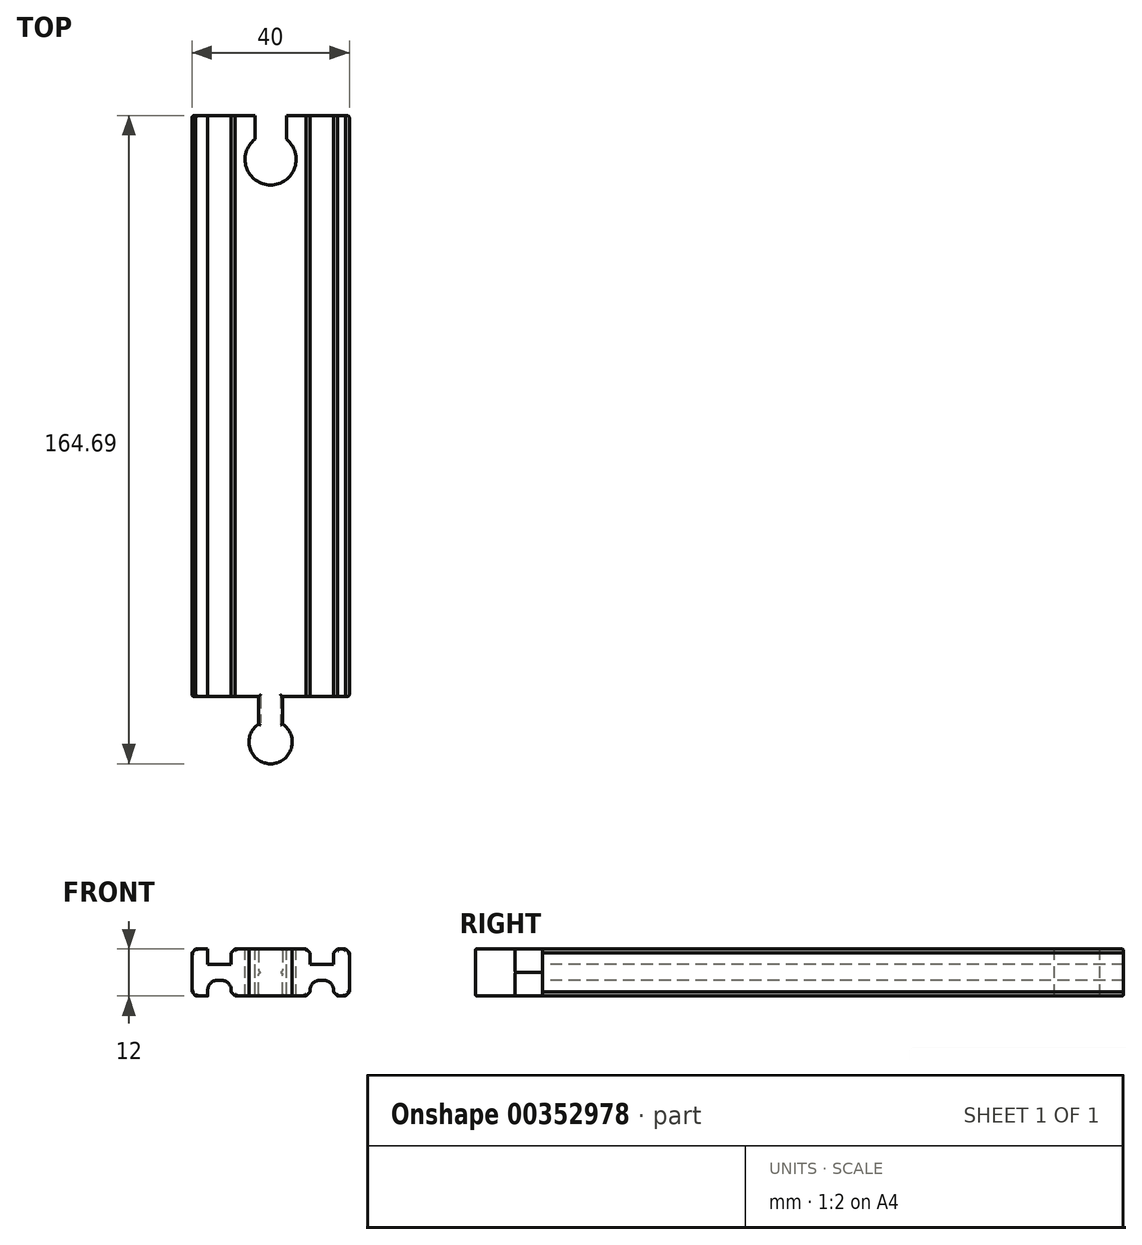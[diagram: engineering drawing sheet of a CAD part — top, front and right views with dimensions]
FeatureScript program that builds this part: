
annotation { "Feature Type Name" : "Feature", "Feature Type Description" : "" }
export const myFeature = defineFeature(function(context is Context, id is Id, definition is map)
    precondition{}
    {
        {
            var Q0;
            Q0=qCreatedBy(makeId("Top.planeOp"),FACE);
            var sketch = newSketch(context, id + "F0", { "sketchPlane" : qUnion([Q0])});
            skLineSegment(sketch, "E0.bottom", {"start": v(20, 73.79) * mm, "end": v(-20, 73.79) * mm});
            skLineSegment(sketch, "E0.top", {"start": v(20, -73.79) * mm, "end": v(-20, -73.79) * mm});
            skLineSegment(sketch, "E0.left", {"start": v(20, 73.79) * mm, "end": v(20, -73.79) * mm});
            skLineSegment(sketch, "E0.right", {"start": v(-20, 73.79) * mm, "end": v(-20, -73.79) * mm});
            skPoint(sketch, "E0.middle", {"position": v(0, 0) * mm});
            skLineSegment(sketch, "E1", {"start": v(-3, -73.79) * mm, "end": v(-3, -80.79) * mm});
            skLineSegment(sketch, "E2", {"start": v(3, -73.79) * mm, "end": v(3, -80.79) * mm});
            skCircle(sketch, "E3", {"center": v(0, -85.4) * mm, "radius": 5.5 * mm});
            skPoint(sketch, "E3.centerSnap0", {"position": v(0, -73.79) * mm});
            skSolve(sketch);
        }
        {
            var Q0;
            Q0=makeQuery(id+"F0.imprint","IMPRINT",FACE,{"disambiguationData":[TD([[makeQuery(id+"F0.imprint","IMPRINT",EDGE,{"derivedFrom":sQuery(id+"F0.wireOp",EDGE,"E0.bottom")}),1.0]])]});
            var Q1;
            {var subQ0=sQuery(id+"F0.wireOp",EDGE,"E1");Q1=makeQuery(id+"F0.imprint","IMPRINT",FACE,{"disambiguationData":[TD([[makeQuery(id+"F0.imprint","IMPRINT",EDGE,{"derivedFrom":subQ0}),1.0]])]});}
            var Q2;
            {var subQ0=sQuery(id+"F0.wireOp",EDGE,"E3");var subQ1=makeQuery(id+"F0.imprint","INTERSECT",VERTEX,{"derivedFrom":[sQuery(id+"F0.wireOp",EDGE,"E1"),subQ0]});Q2=makeQuery(id+"F0.imprint","IMPRINT",FACE,{"disambiguationData":[TD([[makeQuery(id+"F0.imprint","IMPRINT",EDGE,{"disambiguationData":[TD([[subQ1,1.0]])],"derivedFrom":subQ0}),1.0]])]});}
            extrude(context, id + "F1", {"entities" : qUnion([Q0, Q1, Q2]), "offsetDistance" : 25 * mm, "depth" : 6 * mm});
        }
        {
            var Q0;
            Q0=makeQuery(id+"F1.opExtrude","CAP_FACE",FACE,{"disambiguationData":[OSD([sQuery(id+"F0.wireOp",EDGE,"E0.bottom"),sQuery(id+"F0.wireOp",EDGE,"E0.top"),sQuery(id+"F0.wireOp",EDGE,"E0.left"),sQuery(id+"F0.wireOp",EDGE,"E0.right"),sQuery(id+"F0.wireOp",EDGE,"E1"),sQuery(id+"F0.wireOp",EDGE,"E2"),sQuery(id+"F0.wireOp",EDGE,"E3")])],"isStart":false});
            var sketch = newSketch(context, id + "F2", { "sketchPlane" : qUnion([Q0])});
            skLineSegment(sketch, "E4", {"start": v(-4, 73.79) * mm, "end": v(-4, 67.79) * mm});
            skLineSegment(sketch, "E5", {"start": v(4, 73.79) * mm, "end": v(4, 67.79) * mm});
            skCircle(sketch, "E6", {"center": v(0, 62.66) * mm, "radius": 6.5 * mm});
            skSolve(sketch);
        }
        {
            var Q0;
            {var subQ0=sQuery(id+"F2.wireOp",EDGE,"E6");var subQ1=makeQuery(id+"F2.imprint","INTERSECT",VERTEX,{"derivedFrom":[sQuery(id+"F2.wireOp",EDGE,"E4"),subQ0]});Q0=makeQuery(id+"F2.imprint","IMPRINT",FACE,{"disambiguationData":[TD([[makeQuery(id+"F2.imprint","IMPRINT",EDGE,{"disambiguationData":[TD([[subQ1,1.0]])],"derivedFrom":subQ0}),1.0]])]});}
            var Q1;
            {var subQ0=sQuery(id+"F2.wireOp",EDGE,"E4");Q1=makeQuery(id+"F2.imprint","IMPRINT",FACE,{"disambiguationData":[TD([[makeQuery(id+"F2.imprint","IMPRINT",EDGE,{"derivedFrom":subQ0}),1.0]])]});}
            extrude(context, id + "F3", {"entities" : qUnion([Q0, Q1]), "operationType" : NewBodyOperationType.REMOVE, "oppositeDirection" : true, "depth" : 12 * mm});
        }
        {
            var Q0;
            Q0=makeQuery(id+"F1.opExtrude","CAP_FACE",FACE,{"disambiguationData":[OSD([sQuery(id+"F0.wireOp",EDGE,"E0.bottom"),sQuery(id+"F0.wireOp",EDGE,"E0.top"),sQuery(id+"F0.wireOp",EDGE,"E0.left"),sQuery(id+"F0.wireOp",EDGE,"E0.right"),sQuery(id+"F0.wireOp",EDGE,"E1"),sQuery(id+"F0.wireOp",EDGE,"E2"),sQuery(id+"F0.wireOp",EDGE,"E3")])],"isStart":false});
            var sketch = newSketch(context, id + "F4", { "sketchPlane" : qUnion([Q0])});
            skLineSegment(sketch, "E7.bottom", {"start": v(-16, 73.79) * mm, "end": v(-10, 73.79) * mm});
            skLineSegment(sketch, "E7.top", {"start": v(-16, -73.79) * mm, "end": v(-10, -73.79) * mm});
            skLineSegment(sketch, "E7.left", {"start": v(-16, 73.79) * mm, "end": v(-16, -73.79) * mm});
            skLineSegment(sketch, "E7.right", {"start": v(-10, 73.79) * mm, "end": v(-10, -73.79) * mm});
            skLineSegment(sketch, "E8.bottom", {"start": v(10, 73.79) * mm, "end": v(16, 73.79) * mm});
            skLineSegment(sketch, "E8.top", {"start": v(10, -73.79) * mm, "end": v(16, -73.79) * mm});
            skLineSegment(sketch, "E8.left", {"start": v(10, 73.79) * mm, "end": v(10, -73.79) * mm});
            skLineSegment(sketch, "E8.right", {"start": v(16, 73.79) * mm, "end": v(16, -73.79) * mm});
            skSolve(sketch);
        }
        {
            var Q0;
            Q0 = qSketchRegion(id + "F4", true);
            extrude(context, id + "F5", {"entities" : qUnion([Q0]), "operationType" : NewBodyOperationType.REMOVE, "oppositeDirection" : true, "depth" : 4 * mm});
        }
        {
            var Q0;
            Q0=makeQuery(id+"F1.opExtrude","CAP_EDGE",EDGE,{"disambiguationData":[OSD([sQuery(id+"F0.wireOp",EDGE,"E0.right")])],"isStart":false});
            var Q1;
            Q1=makeQuery(id+"F5.boolean.opBoolean","COPY",EDGE,{"derivedFrom":makeQuery(id+"F5.opExtrude","CAP_EDGE",EDGE,{"disambiguationData":[OSD([sQuery(id+"F4.wireOp",EDGE,"E7.left")])],"isStart":true})});
            var Q2;
            Q2=makeQuery(id+"F5.boolean.opBoolean","COPY",EDGE,{"derivedFrom":makeQuery(id+"F5.opExtrude","CAP_EDGE",EDGE,{"disambiguationData":[OSD([sQuery(id+"F4.wireOp",EDGE,"E7.right")])],"isStart":true})});
            var Q3;
            Q3=makeQuery(id+"F5.boolean.opBoolean","COPY",EDGE,{"derivedFrom":makeQuery(id+"F5.opExtrude","CAP_EDGE",EDGE,{"disambiguationData":[OSD([sQuery(id+"F4.wireOp",EDGE,"E8.right")])],"isStart":true})});
            var Q4;
            Q4=makeQuery(id+"F1.opExtrude","CAP_EDGE",EDGE,{"disambiguationData":[OSD([sQuery(id+"F0.wireOp",EDGE,"E0.left")])],"isStart":false});
            var Q5;
            Q5=makeQuery(id+"F5.boolean.opBoolean","COPY",EDGE,{"derivedFrom":makeQuery(id+"F5.opExtrude","CAP_EDGE",EDGE,{"disambiguationData":[OSD([sQuery(id+"F4.wireOp",EDGE,"E8.left")])],"isStart":true})});
            chamfer(context, id + "F6", {"entities" : qUnion([Q0, Q1, Q2, Q3, Q4, Q5]), "width" : 1 * mm, "tangentPropagation" : true});
        }
        {
            var Q0;
            Q0=makeQuery(id+"F1.opExtrude","CAP_EDGE",EDGE,{"disambiguationData":[OSD([sQuery(id+"F0.wireOp",EDGE,"E3")])],"isStart":false});
            var Q1;
            Q1=makeQuery(id+"F1.opExtrude","CAP_EDGE",EDGE,{"disambiguationData":[OSD([sQuery(id+"F0.wireOp",EDGE,"E1")])],"isStart":true});
            var Q2;
            Q2=makeQuery(id+"F1.opExtrude","CAP_EDGE",EDGE,{"disambiguationData":[OSD([sQuery(id+"F0.wireOp",EDGE,"E2")])],"isStart":true});
            var Q3;
            Q3=makeQuery(id+"F1.opExtrude","CAP_EDGE",EDGE,{"disambiguationData":[OSD([sQuery(id+"F0.wireOp",EDGE,"E1")])],"isStart":false});
            var Q4;
            Q4=makeQuery(id+"F1.opExtrude","CAP_EDGE",EDGE,{"disambiguationData":[OSD([sQuery(id+"F0.wireOp",EDGE,"E2")])],"isStart":false});
            var Q5;
            Q5=makeQuery(id+"F3.boolean.opBoolean","COPY",EDGE,{"derivedFrom":makeQuery(id+"F3.opExtrude","CAP_EDGE",EDGE,{"disambiguationData":[OSD([sQuery(id+"F2.wireOp",EDGE,"E6")])],"isStart":true})});
            var Q6;
            Q6=makeQuery(id+"F3.boolean.opBoolean","COPY",EDGE,{"derivedFrom":makeQuery(id+"F3.opExtrude","CAP_EDGE",EDGE,{"disambiguationData":[OSD([sQuery(id+"F2.wireOp",EDGE,"E4")])],"isStart":true})});
            var Q7;
            Q7=makeQuery(id+"F3.boolean.opBoolean","COPY",EDGE,{"derivedFrom":makeQuery(id+"F3.opExtrude","CAP_EDGE",EDGE,{"disambiguationData":[OSD([sQuery(id+"F2.wireOp",EDGE,"E5")])],"isStart":true})});
            var Q8;
            Q8=makeQuery(id+"F3.boolean.opBoolean","COPY",EDGE,{"derivedFrom":makeQuery(id+"F3.opExtrude","CAP_EDGE",EDGE,{"disambiguationData":[OSD([sQuery(id+"F2.wireOp",EDGE,"E4")])],"isStart":false})});
            var Q9;
            Q9=makeQuery(id+"F3.boolean.opBoolean","COPY",EDGE,{"derivedFrom":makeQuery(id+"F3.opExtrude","CAP_EDGE",EDGE,{"disambiguationData":[OSD([sQuery(id+"F2.wireOp",EDGE,"E5")])],"isStart":false})});
            var Q10;
            Q10=makeQuery(id+"F3.boolean.opBoolean","COPY",EDGE,{"derivedFrom":makeQuery(id+"F3.opExtrude","CAP_EDGE",EDGE,{"disambiguationData":[OSD([sQuery(id+"F2.wireOp",EDGE,"E6")])],"isStart":false})});
            var Q11;
            Q11=makeQuery(id+"F1.opExtrude","SWEPT_EDGE",EDGE,{"disambiguationData":[OSD([sQuery(id+"F0.wireOp",EDGE,"E0.top"),sQuery(id+"F0.wireOp",EDGE,"E0.right")])]});
            var Q12;
            {var subQ0=sQuery(id+"F0.wireOp",EDGE,"E0.right");var subQ1=sQuery(id+"F0.wireOp",EDGE,"E0.top");Q12=makeQuery(id+"F6.opChamfer","BLEND_EDGE",EDGE,{"blendedFrom":[makeQuery(id+"F1.opExtrude","CAP_EDGE",EDGE,{"disambiguationData":[OSD([subQ0])],"isStart":false}),makeQuery(id+"F1.opExtrude","SWEPT_FACE",FACE,{"disambiguationData":[OSD([subQ1]),TDD([makeQuery(id+"F0.imprint","IMPRINT",EDGE,{"disambiguationData":[TD([[makeQuery(id+"F0.imprint","INTERSECT",VERTEX,{"derivedFrom":[subQ1,subQ0]}),1.0]])],"derivedFrom":subQ1})])]})],"blendedInto":[makeQuery(id+"F1.opExtrude","SWEPT_FACE",FACE,{"disambiguationData":[OSD([subQ1]),TDD([makeQuery(id+"F0.imprint","IMPRINT",EDGE,{"disambiguationData":[TD([[makeQuery(id+"F0.imprint","INTERSECT",VERTEX,{"derivedFrom":[subQ1,subQ0]}),1.0]])],"derivedFrom":subQ1})])]})]});}
            var Q13;
            Q13=makeQuery(id+"F5.boolean.opBoolean","COPY",EDGE,{"derivedFrom":makeQuery(id+"F5.opExtrude","CAP_EDGE",EDGE,{"disambiguationData":[OSD([sQuery(id+"F4.wireOp",EDGE,"E7.top")])],"isStart":false})});
            var Q14;
            Q14=makeQuery(id+"F5.boolean.opBoolean","COPY",EDGE,{"derivedFrom":makeQuery(id+"F5.opExtrude","SWEPT_EDGE",EDGE,{"disambiguationData":[OSD([sQuery(id+"F0.wireOp",EDGE,"E0.top"),sQuery(id+"F4.wireOp",EDGE,"E7.top"),sQuery(id+"F4.wireOp",EDGE,"E7.left")])]})});
            var Q15;
            {var subQ0=sQuery(id+"F0.wireOp",EDGE,"E0.top");Q15=makeQuery(id+"F6.opChamfer","BLEND_EDGE",EDGE,{"blendedFrom":[makeQuery(id+"F5.boolean.opBoolean","COPY",EDGE,{"derivedFrom":makeQuery(id+"F5.opExtrude","CAP_EDGE",EDGE,{"disambiguationData":[OSD([sQuery(id+"F4.wireOp",EDGE,"E7.left")])],"isStart":true})}),makeQuery(id+"F1.opExtrude","SWEPT_FACE",FACE,{"disambiguationData":[OSD([subQ0]),TDD([makeQuery(id+"F0.imprint","IMPRINT",EDGE,{"disambiguationData":[TD([[makeQuery(id+"F0.imprint","INTERSECT",VERTEX,{"derivedFrom":[subQ0,sQuery(id+"F0.wireOp",EDGE,"E0.right")]}),1.0]])],"derivedFrom":subQ0})])]})],"blendedInto":[makeQuery(id+"F1.opExtrude","SWEPT_FACE",FACE,{"disambiguationData":[OSD([subQ0]),TDD([makeQuery(id+"F0.imprint","IMPRINT",EDGE,{"disambiguationData":[TD([[makeQuery(id+"F0.imprint","INTERSECT",VERTEX,{"derivedFrom":[subQ0,sQuery(id+"F0.wireOp",EDGE,"E0.right")]}),1.0]])],"derivedFrom":subQ0})])]})]});}
            var Q16;
            {var subQ1=sQuery(id+"F0.wireOp",EDGE,"E0.right");var subQ2=sQuery(id+"F0.wireOp",EDGE,"E0.top");var subQ3=makeQuery(id+"F0.imprint","IMPRINT",EDGE,{"disambiguationData":[TD([[makeQuery(id+"F0.imprint","INTERSECT",VERTEX,{"derivedFrom":[subQ2,subQ1]}),1.0]])],"derivedFrom":subQ2});Q16=makeQuery(id+"F5.boolean.opBoolean","SPLIT",EDGE,{"disambiguationData":[TD([makeQuery(id+"F1.opExtrude","SWEPT_FACE",FACE,{"disambiguationData":[OSD([subQ1])]})])],"derivedFrom":makeQuery(id+"F1.opExtrude","CAP_EDGE",EDGE,{"disambiguationData":[OSD([subQ2]),TDD([subQ3])],"isStart":false})});}
            var Q17;
            Q17=makeQuery(id+"F5.boolean.opBoolean","COPY",EDGE,{"derivedFrom":makeQuery(id+"F5.opExtrude","SWEPT_EDGE",EDGE,{"disambiguationData":[OSD([sQuery(id+"F0.wireOp",EDGE,"E0.top"),sQuery(id+"F4.wireOp",EDGE,"E7.top"),sQuery(id+"F4.wireOp",EDGE,"E7.right")])]})});
            var Q18;
            {var subQ0=sQuery(id+"F0.wireOp",EDGE,"E0.top");Q18=makeQuery(id+"F6.opChamfer","BLEND_EDGE",EDGE,{"blendedFrom":[makeQuery(id+"F5.boolean.opBoolean","COPY",EDGE,{"derivedFrom":makeQuery(id+"F5.opExtrude","CAP_EDGE",EDGE,{"disambiguationData":[OSD([sQuery(id+"F4.wireOp",EDGE,"E7.right")])],"isStart":true})}),makeQuery(id+"F1.opExtrude","SWEPT_FACE",FACE,{"disambiguationData":[OSD([subQ0]),TDD([makeQuery(id+"F0.imprint","IMPRINT",EDGE,{"disambiguationData":[TD([[makeQuery(id+"F0.imprint","INTERSECT",VERTEX,{"derivedFrom":[subQ0,sQuery(id+"F0.wireOp",EDGE,"E0.right")]}),1.0]])],"derivedFrom":subQ0})])]})],"blendedInto":[makeQuery(id+"F1.opExtrude","SWEPT_FACE",FACE,{"disambiguationData":[OSD([subQ0]),TDD([makeQuery(id+"F0.imprint","IMPRINT",EDGE,{"disambiguationData":[TD([[makeQuery(id+"F0.imprint","INTERSECT",VERTEX,{"derivedFrom":[subQ0,sQuery(id+"F0.wireOp",EDGE,"E0.right")]}),1.0]])],"derivedFrom":subQ0})])]})]});}
            var Q19;
            {var subQ0=sQuery(id+"F0.wireOp",EDGE,"E1");var subQ1=sQuery(id+"F0.wireOp",EDGE,"E0.right");var subQ2=sQuery(id+"F0.wireOp",EDGE,"E0.top");var subQ3=makeQuery(id+"F0.imprint","IMPRINT",EDGE,{"disambiguationData":[TD([[makeQuery(id+"F0.imprint","INTERSECT",VERTEX,{"derivedFrom":[subQ2,subQ1]}),1.0]])],"derivedFrom":subQ2});Q19=makeQuery(id+"F5.boolean.opBoolean","SPLIT",EDGE,{"disambiguationData":[TD([makeQuery(id+"F1.opExtrude","SWEPT_FACE",FACE,{"disambiguationData":[OSD([subQ0])]})])],"derivedFrom":makeQuery(id+"F1.opExtrude","CAP_EDGE",EDGE,{"disambiguationData":[OSD([subQ2]),TDD([subQ3])],"isStart":false})});}
            var Q20;
            {var subQ0=sQuery(id+"F0.wireOp",EDGE,"E2");var subQ1=sQuery(id+"F0.wireOp",EDGE,"E0.left");var subQ2=sQuery(id+"F0.wireOp",EDGE,"E0.top");var subQ3=makeQuery(id+"F0.imprint","IMPRINT",EDGE,{"disambiguationData":[TD([[makeQuery(id+"F0.imprint","INTERSECT",VERTEX,{"derivedFrom":[subQ2,subQ1]}),-1.0]])],"derivedFrom":subQ2});Q20=makeQuery(id+"F5.boolean.opBoolean","SPLIT",EDGE,{"disambiguationData":[TD([makeQuery(id+"F1.opExtrude","SWEPT_FACE",FACE,{"disambiguationData":[OSD([subQ0])]})])],"derivedFrom":makeQuery(id+"F1.opExtrude","CAP_EDGE",EDGE,{"disambiguationData":[OSD([subQ2]),TDD([subQ3])],"isStart":false})});}
            var Q21;
            {var subQ0=sQuery(id+"F0.wireOp",EDGE,"E0.top");Q21=makeQuery(id+"F6.opChamfer","BLEND_EDGE",EDGE,{"blendedFrom":[makeQuery(id+"F5.boolean.opBoolean","COPY",EDGE,{"derivedFrom":makeQuery(id+"F5.opExtrude","CAP_EDGE",EDGE,{"disambiguationData":[OSD([sQuery(id+"F4.wireOp",EDGE,"E8.left")])],"isStart":true})}),makeQuery(id+"F1.opExtrude","SWEPT_FACE",FACE,{"disambiguationData":[OSD([subQ0]),TDD([makeQuery(id+"F0.imprint","IMPRINT",EDGE,{"disambiguationData":[TD([[makeQuery(id+"F0.imprint","INTERSECT",VERTEX,{"derivedFrom":[subQ0,sQuery(id+"F0.wireOp",EDGE,"E0.left")]}),-1.0]])],"derivedFrom":subQ0})])]})],"blendedInto":[makeQuery(id+"F1.opExtrude","SWEPT_FACE",FACE,{"disambiguationData":[OSD([subQ0]),TDD([makeQuery(id+"F0.imprint","IMPRINT",EDGE,{"disambiguationData":[TD([[makeQuery(id+"F0.imprint","INTERSECT",VERTEX,{"derivedFrom":[subQ0,sQuery(id+"F0.wireOp",EDGE,"E0.left")]}),-1.0]])],"derivedFrom":subQ0})])]})]});}
            var Q22;
            Q22=makeQuery(id+"F5.boolean.opBoolean","COPY",EDGE,{"derivedFrom":makeQuery(id+"F5.opExtrude","SWEPT_EDGE",EDGE,{"disambiguationData":[OSD([sQuery(id+"F0.wireOp",EDGE,"E0.top"),sQuery(id+"F4.wireOp",EDGE,"E8.top"),sQuery(id+"F4.wireOp",EDGE,"E8.left")])]})});
            var Q23;
            Q23=makeQuery(id+"F5.boolean.opBoolean","COPY",EDGE,{"derivedFrom":makeQuery(id+"F5.opExtrude","CAP_EDGE",EDGE,{"disambiguationData":[OSD([sQuery(id+"F4.wireOp",EDGE,"E8.top")])],"isStart":false})});
            var Q24;
            Q24=makeQuery(id+"F5.boolean.opBoolean","COPY",EDGE,{"derivedFrom":makeQuery(id+"F5.opExtrude","SWEPT_EDGE",EDGE,{"disambiguationData":[OSD([sQuery(id+"F0.wireOp",EDGE,"E0.top"),sQuery(id+"F4.wireOp",EDGE,"E8.top"),sQuery(id+"F4.wireOp",EDGE,"E8.right")])]})});
            var Q25;
            {var subQ1=sQuery(id+"F0.wireOp",EDGE,"E0.left");var subQ2=sQuery(id+"F0.wireOp",EDGE,"E0.top");var subQ3=makeQuery(id+"F0.imprint","IMPRINT",EDGE,{"disambiguationData":[TD([[makeQuery(id+"F0.imprint","INTERSECT",VERTEX,{"derivedFrom":[subQ2,subQ1]}),-1.0]])],"derivedFrom":subQ2});Q25=makeQuery(id+"F5.boolean.opBoolean","SPLIT",EDGE,{"disambiguationData":[TD([makeQuery(id+"F1.opExtrude","SWEPT_FACE",FACE,{"disambiguationData":[OSD([subQ1])]})])],"derivedFrom":makeQuery(id+"F1.opExtrude","CAP_EDGE",EDGE,{"disambiguationData":[OSD([subQ2]),TDD([subQ3])],"isStart":false})});}
            var Q26;
            {var subQ0=sQuery(id+"F0.wireOp",EDGE,"E0.left");var subQ1=sQuery(id+"F0.wireOp",EDGE,"E0.top");Q26=makeQuery(id+"F6.opChamfer","BLEND_EDGE",EDGE,{"blendedFrom":[makeQuery(id+"F1.opExtrude","CAP_EDGE",EDGE,{"disambiguationData":[OSD([subQ0])],"isStart":false}),makeQuery(id+"F1.opExtrude","SWEPT_FACE",FACE,{"disambiguationData":[OSD([subQ1]),TDD([makeQuery(id+"F0.imprint","IMPRINT",EDGE,{"disambiguationData":[TD([[makeQuery(id+"F0.imprint","INTERSECT",VERTEX,{"derivedFrom":[subQ1,subQ0]}),-1.0]])],"derivedFrom":subQ1})])]})],"blendedInto":[makeQuery(id+"F1.opExtrude","SWEPT_FACE",FACE,{"disambiguationData":[OSD([subQ1]),TDD([makeQuery(id+"F0.imprint","IMPRINT",EDGE,{"disambiguationData":[TD([[makeQuery(id+"F0.imprint","INTERSECT",VERTEX,{"derivedFrom":[subQ1,subQ0]}),-1.0]])],"derivedFrom":subQ1})])]})]});}
            var Q27;
            Q27=makeQuery(id+"F1.opExtrude","SWEPT_EDGE",EDGE,{"disambiguationData":[OSD([sQuery(id+"F0.wireOp",EDGE,"E0.top"),sQuery(id+"F0.wireOp",EDGE,"E0.left")])]});
            var Q28;
            {var subQ0=sQuery(id+"F0.wireOp",EDGE,"E0.top");Q28=makeQuery(id+"F6.opChamfer","BLEND_EDGE",EDGE,{"blendedFrom":[makeQuery(id+"F5.boolean.opBoolean","COPY",EDGE,{"derivedFrom":makeQuery(id+"F5.opExtrude","CAP_EDGE",EDGE,{"disambiguationData":[OSD([sQuery(id+"F4.wireOp",EDGE,"E8.right")])],"isStart":true})}),makeQuery(id+"F1.opExtrude","SWEPT_FACE",FACE,{"disambiguationData":[OSD([subQ0]),TDD([makeQuery(id+"F0.imprint","IMPRINT",EDGE,{"disambiguationData":[TD([[makeQuery(id+"F0.imprint","INTERSECT",VERTEX,{"derivedFrom":[subQ0,sQuery(id+"F0.wireOp",EDGE,"E0.left")]}),-1.0]])],"derivedFrom":subQ0})])]})],"blendedInto":[makeQuery(id+"F1.opExtrude","SWEPT_FACE",FACE,{"disambiguationData":[OSD([subQ0]),TDD([makeQuery(id+"F0.imprint","IMPRINT",EDGE,{"disambiguationData":[TD([[makeQuery(id+"F0.imprint","INTERSECT",VERTEX,{"derivedFrom":[subQ0,sQuery(id+"F0.wireOp",EDGE,"E0.left")]}),-1.0]])],"derivedFrom":subQ0})])]})]});}
            var Q29;
            Q29=makeQuery(id+"F1.opExtrude","SWEPT_EDGE",EDGE,{"disambiguationData":[OSD([sQuery(id+"F0.wireOp",EDGE,"E0.bottom"),sQuery(id+"F0.wireOp",EDGE,"E0.left")])]});
            var Q30;
            {var subQ4=sQuery(id+"F0.wireOp",EDGE,"E0.left");var subQ6=sQuery(id+"F0.wireOp",EDGE,"E0.bottom");Q30=makeQuery(id+"F6.opChamfer","BLEND_EDGE",EDGE,{"blendedFrom":[makeQuery(id+"F1.opExtrude","CAP_EDGE",EDGE,{"disambiguationData":[OSD([subQ4])],"isStart":false}),makeQuery(id+"F3.boolean.opBoolean","SPLIT",FACE,{"disambiguationData":[TD([makeQuery(id+"F1.opExtrude","SWEPT_FACE",FACE,{"disambiguationData":[OSD([subQ4])]})])],"derivedFrom":makeQuery(id+"F1.opExtrude","SWEPT_FACE",FACE,{"disambiguationData":[OSD([subQ6])]})})],"blendedInto":[makeQuery(id+"F3.boolean.opBoolean","SPLIT",FACE,{"disambiguationData":[TD([makeQuery(id+"F1.opExtrude","SWEPT_FACE",FACE,{"disambiguationData":[OSD([subQ4])]})])],"derivedFrom":makeQuery(id+"F1.opExtrude","SWEPT_FACE",FACE,{"disambiguationData":[OSD([subQ6])]})})]});}
            var Q31;
            {var subQ0=sQuery(id+"F0.wireOp",EDGE,"E0.bottom");var subQ2=sQuery(id+"F0.wireOp",EDGE,"E0.left");var subQ3=makeQuery(id+"F1.opExtrude","SWEPT_FACE",FACE,{"disambiguationData":[OSD([subQ2])]});Q31=makeQuery(id+"F5.boolean.opBoolean","SPLIT",EDGE,{"disambiguationData":[TD([subQ3])],"derivedFrom":makeQuery(id+"F3.boolean.opBoolean","SPLIT",EDGE,{"disambiguationData":[TD([subQ3])],"derivedFrom":makeQuery(id+"F1.opExtrude","CAP_EDGE",EDGE,{"disambiguationData":[OSD([subQ0])],"isStart":false})})});}
            var Q32;
            {var subQ4=sQuery(id+"F0.wireOp",EDGE,"E0.left");var subQ6=sQuery(id+"F0.wireOp",EDGE,"E0.bottom");Q32=makeQuery(id+"F6.opChamfer","BLEND_EDGE",EDGE,{"blendedFrom":[makeQuery(id+"F5.boolean.opBoolean","COPY",EDGE,{"derivedFrom":makeQuery(id+"F5.opExtrude","CAP_EDGE",EDGE,{"disambiguationData":[OSD([sQuery(id+"F4.wireOp",EDGE,"E8.right")])],"isStart":true})}),makeQuery(id+"F3.boolean.opBoolean","SPLIT",FACE,{"disambiguationData":[TD([makeQuery(id+"F1.opExtrude","SWEPT_FACE",FACE,{"disambiguationData":[OSD([subQ4])]})])],"derivedFrom":makeQuery(id+"F1.opExtrude","SWEPT_FACE",FACE,{"disambiguationData":[OSD([subQ6])]})})],"blendedInto":[makeQuery(id+"F3.boolean.opBoolean","SPLIT",FACE,{"disambiguationData":[TD([makeQuery(id+"F1.opExtrude","SWEPT_FACE",FACE,{"disambiguationData":[OSD([subQ4])]})])],"derivedFrom":makeQuery(id+"F1.opExtrude","SWEPT_FACE",FACE,{"disambiguationData":[OSD([subQ6])]})})]});}
            var Q33;
            Q33=makeQuery(id+"F5.boolean.opBoolean","COPY",EDGE,{"derivedFrom":makeQuery(id+"F5.opExtrude","SWEPT_EDGE",EDGE,{"disambiguationData":[OSD([sQuery(id+"F0.wireOp",EDGE,"E0.bottom"),sQuery(id+"F4.wireOp",EDGE,"E8.bottom"),sQuery(id+"F4.wireOp",EDGE,"E8.right")])]})});
            var Q34;
            Q34=makeQuery(id+"F5.boolean.opBoolean","COPY",EDGE,{"derivedFrom":makeQuery(id+"F5.opExtrude","CAP_EDGE",EDGE,{"disambiguationData":[OSD([sQuery(id+"F4.wireOp",EDGE,"E8.bottom")])],"isStart":false})});
            var Q35;
            Q35=makeQuery(id+"F5.boolean.opBoolean","COPY",EDGE,{"derivedFrom":makeQuery(id+"F5.opExtrude","SWEPT_EDGE",EDGE,{"disambiguationData":[OSD([sQuery(id+"F0.wireOp",EDGE,"E0.bottom"),sQuery(id+"F4.wireOp",EDGE,"E8.bottom"),sQuery(id+"F4.wireOp",EDGE,"E8.left")])]})});
            var Q36;
            {var subQ4=sQuery(id+"F0.wireOp",EDGE,"E0.left");var subQ6=sQuery(id+"F0.wireOp",EDGE,"E0.bottom");Q36=makeQuery(id+"F6.opChamfer","BLEND_EDGE",EDGE,{"blendedFrom":[makeQuery(id+"F5.boolean.opBoolean","COPY",EDGE,{"derivedFrom":makeQuery(id+"F5.opExtrude","CAP_EDGE",EDGE,{"disambiguationData":[OSD([sQuery(id+"F4.wireOp",EDGE,"E8.left")])],"isStart":true})}),makeQuery(id+"F3.boolean.opBoolean","SPLIT",FACE,{"disambiguationData":[TD([makeQuery(id+"F1.opExtrude","SWEPT_FACE",FACE,{"disambiguationData":[OSD([subQ4])]})])],"derivedFrom":makeQuery(id+"F1.opExtrude","SWEPT_FACE",FACE,{"disambiguationData":[OSD([subQ6])]})})],"blendedInto":[makeQuery(id+"F3.boolean.opBoolean","SPLIT",FACE,{"disambiguationData":[TD([makeQuery(id+"F1.opExtrude","SWEPT_FACE",FACE,{"disambiguationData":[OSD([subQ4])]})])],"derivedFrom":makeQuery(id+"F1.opExtrude","SWEPT_FACE",FACE,{"disambiguationData":[OSD([subQ6])]})})]});}
            var Q37;
            {var subQ0=sQuery(id+"F0.wireOp",EDGE,"E0.bottom");var subQ2=makeQuery(id+"F3.opExtrude","SWEPT_FACE",FACE,{"disambiguationData":[OSD([sQuery(id+"F2.wireOp",EDGE,"E5")])]});var subQ3=sQuery(id+"F0.wireOp",EDGE,"E0.left");Q37=makeQuery(id+"F5.boolean.opBoolean","SPLIT",EDGE,{"disambiguationData":[TD([makeQuery(id+"F3.boolean.opBoolean","COPY",FACE,{"derivedFrom":subQ2})])],"derivedFrom":makeQuery(id+"F3.boolean.opBoolean","SPLIT",EDGE,{"disambiguationData":[TD([makeQuery(id+"F1.opExtrude","SWEPT_FACE",FACE,{"disambiguationData":[OSD([subQ3])]})])],"derivedFrom":makeQuery(id+"F1.opExtrude","CAP_EDGE",EDGE,{"disambiguationData":[OSD([subQ0])],"isStart":false})})});}
            var Q38;
            {var subQ0=sQuery(id+"F0.wireOp",EDGE,"E0.bottom");var subQ2=sQuery(id+"F0.wireOp",EDGE,"E0.right");var subQ4=makeQuery(id+"F3.opExtrude","SWEPT_FACE",FACE,{"disambiguationData":[OSD([sQuery(id+"F2.wireOp",EDGE,"E4")])]});Q38=makeQuery(id+"F5.boolean.opBoolean","SPLIT",EDGE,{"disambiguationData":[TD([makeQuery(id+"F3.boolean.opBoolean","COPY",FACE,{"derivedFrom":subQ4})])],"derivedFrom":makeQuery(id+"F3.boolean.opBoolean","SPLIT",EDGE,{"disambiguationData":[TD([makeQuery(id+"F1.opExtrude","SWEPT_FACE",FACE,{"disambiguationData":[OSD([subQ2])]})])],"derivedFrom":makeQuery(id+"F1.opExtrude","CAP_EDGE",EDGE,{"disambiguationData":[OSD([subQ0])],"isStart":false})})});}
            var Q39;
            {var subQ3=sQuery(id+"F0.wireOp",EDGE,"E0.right");var subQ6=sQuery(id+"F0.wireOp",EDGE,"E0.bottom");Q39=makeQuery(id+"F6.opChamfer","BLEND_EDGE",EDGE,{"blendedFrom":[makeQuery(id+"F5.boolean.opBoolean","COPY",EDGE,{"derivedFrom":makeQuery(id+"F5.opExtrude","CAP_EDGE",EDGE,{"disambiguationData":[OSD([sQuery(id+"F4.wireOp",EDGE,"E7.right")])],"isStart":true})}),makeQuery(id+"F3.boolean.opBoolean","SPLIT",FACE,{"disambiguationData":[TD([makeQuery(id+"F1.opExtrude","SWEPT_FACE",FACE,{"disambiguationData":[OSD([subQ3])]})])],"derivedFrom":makeQuery(id+"F1.opExtrude","SWEPT_FACE",FACE,{"disambiguationData":[OSD([subQ6])]})})],"blendedInto":[makeQuery(id+"F3.boolean.opBoolean","SPLIT",FACE,{"disambiguationData":[TD([makeQuery(id+"F1.opExtrude","SWEPT_FACE",FACE,{"disambiguationData":[OSD([subQ3])]})])],"derivedFrom":makeQuery(id+"F1.opExtrude","SWEPT_FACE",FACE,{"disambiguationData":[OSD([subQ6])]})})]});}
            var Q40;
            Q40=makeQuery(id+"F5.boolean.opBoolean","COPY",EDGE,{"derivedFrom":makeQuery(id+"F5.opExtrude","SWEPT_EDGE",EDGE,{"disambiguationData":[OSD([sQuery(id+"F0.wireOp",EDGE,"E0.bottom"),sQuery(id+"F4.wireOp",EDGE,"E7.bottom"),sQuery(id+"F4.wireOp",EDGE,"E7.right")])]})});
            var Q41;
            Q41=makeQuery(id+"F5.boolean.opBoolean","COPY",EDGE,{"derivedFrom":makeQuery(id+"F5.opExtrude","CAP_EDGE",EDGE,{"disambiguationData":[OSD([sQuery(id+"F4.wireOp",EDGE,"E7.bottom")])],"isStart":false})});
            var Q42;
            Q42=makeQuery(id+"F5.boolean.opBoolean","COPY",EDGE,{"derivedFrom":makeQuery(id+"F5.opExtrude","SWEPT_EDGE",EDGE,{"disambiguationData":[OSD([sQuery(id+"F0.wireOp",EDGE,"E0.bottom"),sQuery(id+"F4.wireOp",EDGE,"E7.bottom"),sQuery(id+"F4.wireOp",EDGE,"E7.left")])]})});
            var Q43;
            {var subQ3=sQuery(id+"F0.wireOp",EDGE,"E0.right");var subQ6=sQuery(id+"F0.wireOp",EDGE,"E0.bottom");Q43=makeQuery(id+"F6.opChamfer","BLEND_EDGE",EDGE,{"blendedFrom":[makeQuery(id+"F5.boolean.opBoolean","COPY",EDGE,{"derivedFrom":makeQuery(id+"F5.opExtrude","CAP_EDGE",EDGE,{"disambiguationData":[OSD([sQuery(id+"F4.wireOp",EDGE,"E7.left")])],"isStart":true})}),makeQuery(id+"F3.boolean.opBoolean","SPLIT",FACE,{"disambiguationData":[TD([makeQuery(id+"F1.opExtrude","SWEPT_FACE",FACE,{"disambiguationData":[OSD([subQ3])]})])],"derivedFrom":makeQuery(id+"F1.opExtrude","SWEPT_FACE",FACE,{"disambiguationData":[OSD([subQ6])]})})],"blendedInto":[makeQuery(id+"F3.boolean.opBoolean","SPLIT",FACE,{"disambiguationData":[TD([makeQuery(id+"F1.opExtrude","SWEPT_FACE",FACE,{"disambiguationData":[OSD([subQ3])]})])],"derivedFrom":makeQuery(id+"F1.opExtrude","SWEPT_FACE",FACE,{"disambiguationData":[OSD([subQ6])]})})]});}
            var Q44;
            {var subQ3=sQuery(id+"F0.wireOp",EDGE,"E0.right");var subQ6=sQuery(id+"F0.wireOp",EDGE,"E0.bottom");Q44=makeQuery(id+"F6.opChamfer","BLEND_EDGE",EDGE,{"blendedFrom":[makeQuery(id+"F1.opExtrude","CAP_EDGE",EDGE,{"disambiguationData":[OSD([subQ3])],"isStart":false}),makeQuery(id+"F3.boolean.opBoolean","SPLIT",FACE,{"disambiguationData":[TD([makeQuery(id+"F1.opExtrude","SWEPT_FACE",FACE,{"disambiguationData":[OSD([subQ3])]})])],"derivedFrom":makeQuery(id+"F1.opExtrude","SWEPT_FACE",FACE,{"disambiguationData":[OSD([subQ6])]})})],"blendedInto":[makeQuery(id+"F3.boolean.opBoolean","SPLIT",FACE,{"disambiguationData":[TD([makeQuery(id+"F1.opExtrude","SWEPT_FACE",FACE,{"disambiguationData":[OSD([subQ3])]})])],"derivedFrom":makeQuery(id+"F1.opExtrude","SWEPT_FACE",FACE,{"disambiguationData":[OSD([subQ6])]})})]});}
            var Q45;
            Q45=makeQuery(id+"F1.opExtrude","SWEPT_EDGE",EDGE,{"disambiguationData":[OSD([sQuery(id+"F0.wireOp",EDGE,"E0.bottom"),sQuery(id+"F0.wireOp",EDGE,"E0.right")])]});
            var Q46;
            {var subQ0=sQuery(id+"F0.wireOp",EDGE,"E0.bottom");var subQ2=sQuery(id+"F0.wireOp",EDGE,"E0.right");var subQ4=makeQuery(id+"F1.opExtrude","SWEPT_FACE",FACE,{"disambiguationData":[OSD([subQ2])]});Q46=makeQuery(id+"F5.boolean.opBoolean","SPLIT",EDGE,{"disambiguationData":[TD([subQ4])],"derivedFrom":makeQuery(id+"F3.boolean.opBoolean","SPLIT",EDGE,{"disambiguationData":[TD([subQ4])],"derivedFrom":makeQuery(id+"F1.opExtrude","CAP_EDGE",EDGE,{"disambiguationData":[OSD([subQ0])],"isStart":false})})});}
            fillet(context, id + "F7", {"entities" : qUnion([Q0, Q1, Q2, Q3, Q4, Q5, Q6, Q7, Q8, Q9, Q10, Q11, Q12, Q13, Q14, Q15, Q16, Q17, Q18, Q19, Q20, Q21, Q22, Q23, Q24, Q25, Q26, Q27, Q28, Q29, Q30, Q31, Q32, Q33, Q34, Q35, Q36, Q37, Q38, Q39, Q40, Q41, Q42, Q43, Q44, Q45, Q46]), "radius" : 0.5 * mm, "tangentPropagation" : true, "defaultsChanged" : false, "vertexSettings" : [], "allowEdgeOverflow" : false});
        }
        {
            var Q0;
            Q0=makeQuery(id+"F1.opExtrude","SWEPT_BODY",BODY,{"disambiguationData":[OSD([sQuery(id+"F0.wireOp",EDGE,"E0.bottom"),sQuery(id+"F0.wireOp",EDGE,"E0.top"),sQuery(id+"F0.wireOp",EDGE,"E0.left"),sQuery(id+"F0.wireOp",EDGE,"E0.right"),sQuery(id+"F0.wireOp",EDGE,"E1"),sQuery(id+"F0.wireOp",EDGE,"E2"),sQuery(id+"F0.wireOp",EDGE,"E3")])]});
            var Q1;
            Q1=qCreatedBy(makeId("Top.planeOp"),FACE);
            mirror(context, id + "F8", {"operationType" : NewBodyOperationType.ADD, "entities" : qUnion([Q0]), "mirrorPlane" : qUnion([Q1])});
        }
        {
            var Q0;
            Q0=makeQuery(id+"F8.opPattern","COPY",EDGE,{"derivedFrom":makeQuery(id+"F5.boolean.opBoolean","COPY",EDGE,{"derivedFrom":makeQuery(id+"F5.opExtrude","CAP_EDGE",EDGE,{"disambiguationData":[OSD([sQuery(id+"F4.wireOp",EDGE,"E8.right")])],"isStart":false})}),"instanceName":"1"});
            var Q1;
            Q1=makeQuery(id+"F8.opPattern","COPY",EDGE,{"derivedFrom":makeQuery(id+"F5.boolean.opBoolean","COPY",EDGE,{"derivedFrom":makeQuery(id+"F5.opExtrude","CAP_EDGE",EDGE,{"disambiguationData":[OSD([sQuery(id+"F4.wireOp",EDGE,"E8.left")])],"isStart":false})}),"instanceName":"1"});
            var Q2;
            Q2=makeQuery(id+"F8.opPattern","COPY",EDGE,{"derivedFrom":makeQuery(id+"F5.boolean.opBoolean","COPY",EDGE,{"derivedFrom":makeQuery(id+"F5.opExtrude","CAP_EDGE",EDGE,{"disambiguationData":[OSD([sQuery(id+"F4.wireOp",EDGE,"E7.right")])],"isStart":false})}),"instanceName":"1"});
            var Q3;
            Q3=makeQuery(id+"F8.opPattern","COPY",EDGE,{"derivedFrom":makeQuery(id+"F5.boolean.opBoolean","COPY",EDGE,{"derivedFrom":makeQuery(id+"F5.opExtrude","CAP_EDGE",EDGE,{"disambiguationData":[OSD([sQuery(id+"F4.wireOp",EDGE,"E7.left")])],"isStart":false})}),"instanceName":"1"});
            fillet(context, id + "F9", {"entities" : qUnion([Q0, Q1, Q2, Q3]), "tangentPropagation" : true, "radius" : 2.5 * mm, "defaultsChanged" : true, "vertexSettings" : [], "allowEdgeOverflow" : false});
        }
    });
